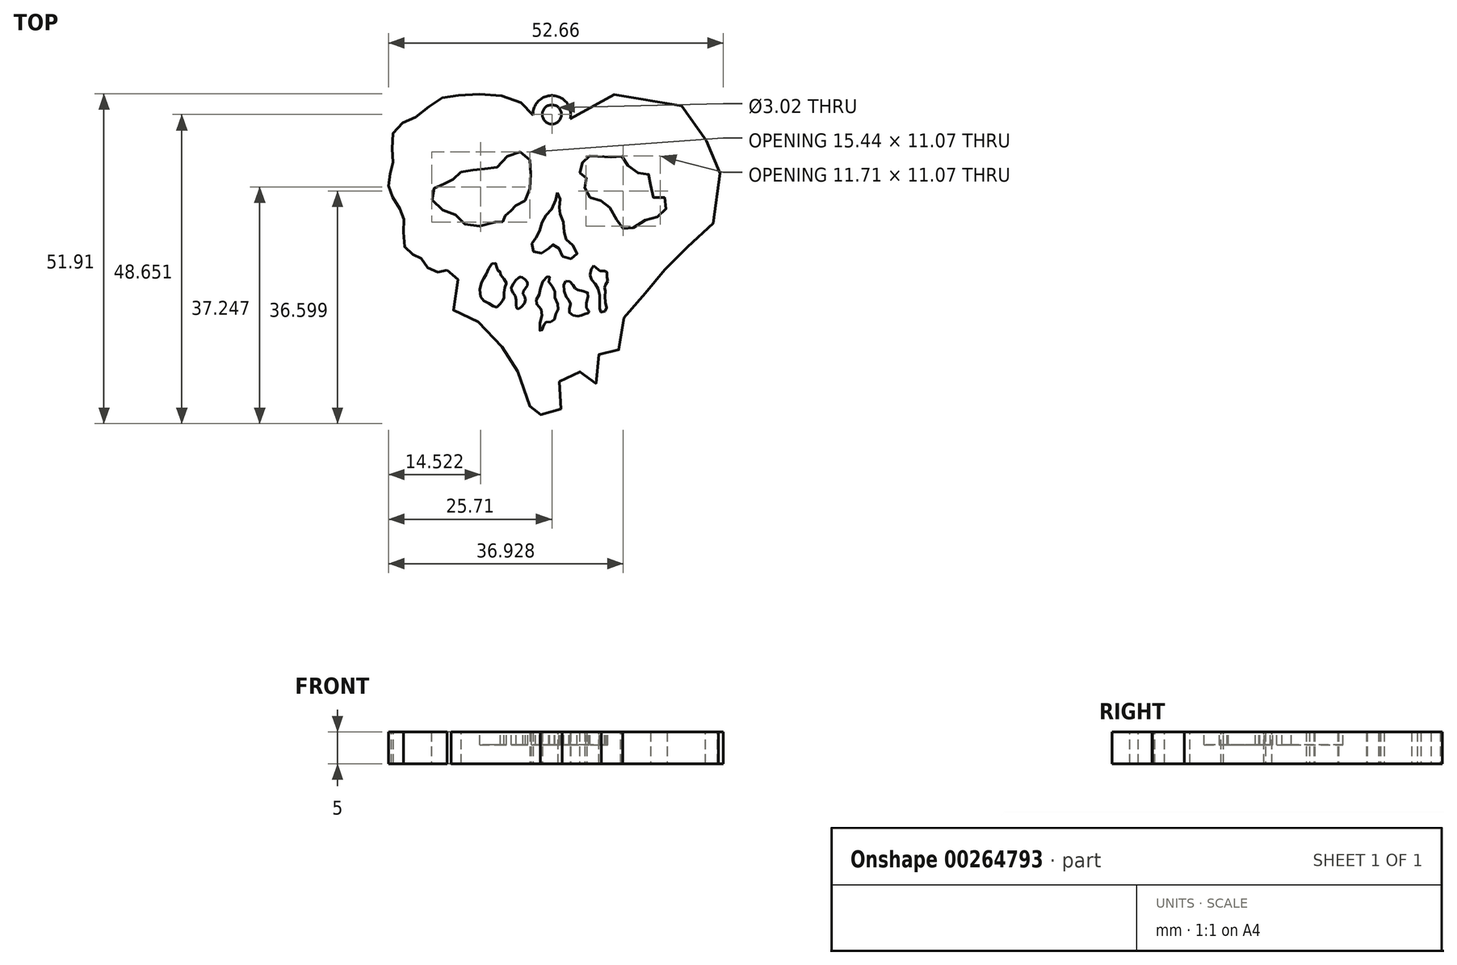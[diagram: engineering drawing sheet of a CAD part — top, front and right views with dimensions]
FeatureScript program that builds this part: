
annotation { "Feature Type Name" : "Feature", "Feature Type Description" : "" }
export const myFeature = defineFeature(function(context is Context, id is Id, definition is map)
    precondition{}
    {
        {
            var Q0;
            Q0=qCreatedBy(makeId("Top.planeOp"),FACE);
            var sketch = newSketch(context, id + "F0", { "sketchPlane" : qUnion([Q0])});
            skLineSegment(sketch, "E0", {"start": v(0.08, 15.96) * mm, "end": v(0.08, -29.04) * mm, "construction": true});
            skFitSpline(sketch, "E1", {"points": [v(0.08, 15.12) * mm, v(1.8, 15.96) * mm, v(5.58, 18.64) * mm, v(10.27, 20.57) * mm, v(19.75, 18.98) * mm, v(24.03, 15.96) * mm, v(24.45, 12.86) * mm, v(26.8, 11.1) * mm, v(26.13, 6.82) * mm, v(26.04, 2.12) * mm, v(23.27, -2.16) * mm, v(21.76, -2.5) * mm, v(21.1, -4.34) * mm, v(19.08, -6.1) * mm, v(17.82, -6.94) * mm, v(17.4, -9.03) * mm, v(15.64, -10.54) * mm, v(14.05, -10.96) * mm, v(13.55, -11.97) * mm, v(11.31, -14.7) * mm, v(10.84, -16.77) * mm, v(11.02, -19.08) * mm, v(9.42, -19.91) * mm, v(8.4, -19.08) * mm, v(7.52, -19.68) * mm, v(7.64, -22.23) * mm, v(7.7, -24.18) * mm, v(6.92, -24.96) * mm, v(6.21, -24.54) * mm, v(5.98, -25.01) * mm, v(5.09, -23.65) * mm, v(3.95, -23.12) * mm, v(3.15, -23.83) * mm, v(2.05, -24.06) * mm, v(1.07, -24.92) * mm, v(1.37, -27.18) * mm, v(1.6, -28.22) * mm, v(1.31, -29.31) * mm, v(0.68, -31) * mm, v(-1.46, -30.7) * mm, v(-1.93, -27.26) * mm, v(-2.64, -27.61) * mm, v(-3.35, -28.5) * mm, v(-4.3, -27.67) * mm, v(-5.2, -23.88) * mm, v(-5.67, -22.34) * mm, v(-6.74, -20.85) * mm, v(-7.62, -19.37) * mm, v(-10.41, -18.13) * mm, v(-11.48, -16) * mm, v(-12.13, -13.86) * mm, v(-14.5, -14.15) * mm, v(-15.75, -12.61) * mm, v(-15.51, -9.65) * mm, v(-15.04, -9) * mm, v(-14.33, -7.33) * mm, v(-14.5, -6.15) * mm, v(-16.46, -7.15) * mm], "startDerivative": vector(95.52, 38.59) * mm, "endDerivative": vector(-155.6, -97.2) * mm});
            skFitSpline(sketch, "E2", {"points": [v(-16.46, -7.15) * mm, v(-17.56, -7.42) * mm, v(-19.07, -7.15) * mm, v(-20.23, -5.85) * mm, v(-20.94, -4.84) * mm, v(-22.37, -4.47) * mm, v(-23.32, -2.82) * mm, v(-23.25, 0) * mm, v(-23.46, 1.56) * mm, v(-24.38, 3.32) * mm, v(-25.54, 5.33) * mm, v(-25.65, 7.1) * mm, v(-25.15, 9) * mm, v(-24.98, 10.83) * mm, v(-25.19, 13.83) * mm, v(-23.58, 15.97) * mm, v(-21.2, 17.06) * mm, v(-18.3, 19.45) * mm, v(-15.24, 20.33) * mm, v(-9.5, 20.5) * mm, v(-4.33, 18.86) * mm, v(-2.15, 16.14) * mm, v(-0.7, 15.1) * mm, v(0.08, 15.12) * mm], "startDerivative": vector(-33.79, -11.1) * mm, "endDerivative": vector(28.69, 5.55) * mm});
            skFitSpline(sketch, "E3", {"points": [v(-15.54, 7.18) * mm, v(-16.93, 6.43) * mm, v(-18.22, 6.03) * mm, v(-18.97, 4.49) * mm, v(-17.48, 2.5) * mm, v(-15.18, 1.6) * mm, v(-13.54, 0) * mm, v(-10.45, 0) * mm, v(-8.2, 0.55) * mm, v(-7.81, 0.5) * mm, v(-7.52, 0.56) * mm, v(-7.36, 1.37) * mm, v(-6.93, 1.67) * mm, v(-6.3, 2.5) * mm, v(-5.9, 2.96) * mm, v(-5.21, 3.13) * mm, v(-3.7, 4.49) * mm, v(-3.46, 7.08) * mm, v(-3.3, 9.72) * mm, v(-4.6, 11.37) * mm, v(-6.9, 10.92) * mm, v(-8.9, 8.87) * mm, v(-10.99, 8.82) * mm, v(-12.63, 8.57) * mm, v(-14.5, 8.18) * mm, v(-15.54, 7.18) * mm]});
            skFitSpline(sketch, "E4", {"points": [v(5.9, 10.84) * mm, v(4.72, 9.72) * mm, v(4.49, 8.06) * mm, v(5.44, 7.34) * mm, v(5.2, 5.8) * mm, v(6.27, 4.14) * mm, v(8.22, 3.6) * mm, v(9.82, 1.53) * mm, v(11.13, -0.54) * mm, v(12.61, -0.54) * mm, v(15.46, 1.06) * mm, v(17.47, 1.65) * mm, v(17.89, 4.2) * mm, v(15.93, 4.32) * mm, v(15.52, 7.17) * mm, v(14.92, 8.06) * mm, v(12.61, 8.47) * mm, v(11.25, 10.66) * mm, v(9.65, 10.66) * mm, v(6.86, 10.84) * mm, v(5.9, 10.84) * mm]});
            skCircle(sketch, "E5", {"center": v(0, 17.36) * mm, "radius": 2.97 * mm});
            skCircle(sketch, "E6", {"center": v(0, 17.36) * mm, "radius": 1.5 * mm});
            skSolve(sketch);
        }
        {
            var Q0;
            Q0=makeQuery(id+"F0.imprint","IMPRINT",FACE,{"disambiguationData":[TD([[makeQuery(id+"F0.imprint","IMPRINT",EDGE,{"derivedFrom":sQuery(id+"F0.wireOp",EDGE,"E1")}),-1.0]])]});
            var Q1;
            Q1=makeQuery(id+"F0.imprint","IMPRINT",FACE,{"disambiguationData":[TD([[makeQuery(id+"F0.imprint","IMPRINT",EDGE,{"derivedFrom":sQuery(id+"F0.wireOp",EDGE,"E3")}),-1.0]])]});
            var Q2;
            Q2=makeQuery(id+"F0.imprint","IMPRINT",FACE,{"disambiguationData":[TD([[makeQuery(id+"F0.imprint","IMPRINT",EDGE,{"derivedFrom":sQuery(id+"F0.wireOp",EDGE,"E6")}),-1.0]])]});
            extrude(context, id + "F1", {"entities" : qUnion([Q0, Q1, Q2]), "depth" : 5 * mm, "offsetDistance" : 25 * mm});
        }
        {
            var Q0;
            Q0=makeQuery(id+"F1.opExtrude","CAP_FACE",FACE,{"disambiguationData":[OSD([sQuery(id+"F0.wireOp",EDGE,"E1"),sQuery(id+"F0.wireOp",EDGE,"E2"),sQuery(id+"F0.wireOp",EDGE,"E3"),sQuery(id+"F0.wireOp",EDGE,"E4")])],"isStart":false});
            var sketch = newSketch(context, id + "F2", { "sketchPlane" : qUnion([Q0])});
            skFitSpline(sketch, "E7", {"points": [v(0.86, 5.03) * mm, v(0.44, 3.23) * mm, v(-0.82, 1.64) * mm, v(-1.66, 0) * mm, v(-2.33, -1.8) * mm, v(-3.13, -2.85) * mm, v(-2.67, -4.4) * mm, v(-0.78, -4.02) * mm, v(0, -3.14) * mm, v(1.06, -3.6) * mm, v(1.99, -5.24) * mm, v(3.92, -4.78) * mm, v(2.9, -2.9) * mm, v(1.99, -1.8) * mm, v(1.78, 0.71) * mm, v(1.15, 2.14) * mm, v(1.32, 3.73) * mm, v(0.86, 5.03) * mm]});
            skFitSpline(sketch, "E8", {"points": [v(-9.41, -6.12) * mm, v(-10.36, -7.87) * mm, v(-11.07, -9) * mm, v(-11.07, -11.6) * mm, v(-9.74, -12.4) * mm, v(-8.76, -12.97) * mm, v(-7.93, -12.11) * mm, v(-7.55, -11.58) * mm, v(-7.52, -10.27) * mm, v(-7.2, -9) * mm, v(-8.08, -7.87) * mm, v(-8.17, -7.3) * mm, v(-8.61, -7.1) * mm, v(-8.76, -6.15) * mm, v(-9.41, -6.12) * mm]});
            skFitSpline(sketch, "E9", {"points": [v(-5.26, -8.35) * mm, v(-6.39, -10.04) * mm, v(-5.68, -11.43) * mm, v(-5.44, -13.21) * mm, v(-4.14, -11.88) * mm, v(-4.55, -10.66) * mm, v(-3.8, -9.33) * mm, v(-4.73, -8.23) * mm, v(-5.26, -8.35) * mm]});
            skFitSpline(sketch, "E10", {"points": [v(-0.76, -8.17) * mm, v(-1.73, -9.71) * mm, v(-2.1, -11.28) * mm, v(-2.56, -12.17) * mm, v(-1.62, -13.39) * mm, v(-1.82, -15.35) * mm, v(-1.8, -16.8) * mm, v(-1.26, -15.97) * mm, v(-1.11, -15.4) * mm, v(-0.46, -15.32) * mm, v(0.34, -14.99) * mm, v(0.64, -13.98) * mm, v(1.08, -12.94) * mm, v(0.46, -11.31) * mm, v(0.37, -10.07) * mm, v(-0.49, -9) * mm, v(-0.34, -8.14) * mm, v(-0.76, -8.17) * mm]});
            skFitSpline(sketch, "E11", {"points": [v(2.2, -8.82) * mm, v(2.1, -11.08) * mm, v(2.95, -12.38) * mm, v(2.77, -13.83) * mm, v(4.26, -14.37) * mm, v(5, -14.09) * mm, v(5.87, -13.77) * mm, v(5.38, -12.85) * mm, v(5.68, -10.75) * mm, v(3.93, -10.22) * mm, v(3.37, -9.47) * mm, v(2.2, -8.82) * mm]});
            skFitSpline(sketch, "E12", {"points": [v(6.57, -6.43) * mm, v(6.06, -7.4) * mm, v(6.25, -8.66) * mm, v(7.1, -9.68) * mm, v(7.53, -11.5) * mm, v(7.53, -13.4) * mm, v(7.89, -13.8) * mm, v(8.6, -13.31) * mm, v(8.4, -12.18) * mm, v(8.41, -10.65) * mm, v(8.3, -9.9) * mm, v(8.41, -9.41) * mm, v(8.77, -8.9) * mm, v(8.66, -8) * mm, v(8.56, -7.27) * mm, v(7.9, -7.33) * mm, v(7.13, -6.94) * mm, v(6.57, -6.43) * mm]});
            skSolve(sketch);
        }
        {
            var Q0;
            Q0=makeQuery(id+"F2.imprint","IMPRINT",FACE,{"disambiguationData":[TD([[makeQuery(id+"F2.imprint","IMPRINT",EDGE,{"derivedFrom":sQuery(id+"F2.wireOp",EDGE,"E7")}),1.0]])]});
            var Q1;
            Q1=makeQuery(id+"F2.imprint","IMPRINT",FACE,{"disambiguationData":[TD([[makeQuery(id+"F2.imprint","IMPRINT",EDGE,{"derivedFrom":sQuery(id+"F2.wireOp",EDGE,"E8")}),1.0]])]});
            var Q2;
            Q2=makeQuery(id+"F2.imprint","IMPRINT",FACE,{"disambiguationData":[TD([[makeQuery(id+"F2.imprint","IMPRINT",EDGE,{"derivedFrom":sQuery(id+"F2.wireOp",EDGE,"E9")}),1.0]])]});
            var Q3;
            Q3=makeQuery(id+"F2.imprint","IMPRINT",FACE,{"disambiguationData":[TD([[makeQuery(id+"F2.imprint","IMPRINT",EDGE,{"derivedFrom":sQuery(id+"F2.wireOp",EDGE,"E10")}),1.0]])]});
            var Q4;
            Q4=makeQuery(id+"F2.imprint","IMPRINT",FACE,{"disambiguationData":[TD([[makeQuery(id+"F2.imprint","IMPRINT",EDGE,{"derivedFrom":sQuery(id+"F2.wireOp",EDGE,"E11")}),1.0]])]});
            var Q5;
            Q5=makeQuery(id+"F2.imprint","IMPRINT",FACE,{"disambiguationData":[TD([[makeQuery(id+"F2.imprint","IMPRINT",EDGE,{"derivedFrom":sQuery(id+"F2.wireOp",EDGE,"E12")}),1.0]])]});
            extrude(context, id + "F3", {"entities" : qUnion([Q0, Q1, Q2, Q3, Q4, Q5]), "operationType" : NewBodyOperationType.REMOVE, "oppositeDirection" : true, "depth" : 2 * mm, "offsetDistance" : 25 * mm});
        }
    });
